# Revit family: Hager-Univers-IP65-D300-H550-Cl.II-encl-PL-en
name_source: partatom
category: Equipement électrique
units: mm (PartAtom-declared; Revit-internal decimal feet)

## family parameters
Configuration du panneau = Deux colonnes, circuits au sein
Cote de connecteur circulaire = Utiliser le diamètre
Couper avec des vides une fois chargée = Non
Hôte = Face
Partagée = Non
Point de calcul de pièce = Non
Type d'élément = Tableau de raccordement

## types (6) — shared parameters
Commentaires du type = Univers
EF000003 - Mounting method = EV000384 - Surface mounted (plaster)
EF000007 - Colour = EV000270 - Grey
EF000040 - Height = 550 mm
EF000049 - Depth = 300 mm  [stored 0.984252 ft]
EF000116 - RAL-number = 7035
EF000118 - With mounting plate = Non
EF000266 - Number of rows = 3
EF001088 - Extension possible = Non
EF001131 - Internal depth = 150 mm  [stored 0.492126 ft]
EF001596 - Material housing = EV000139 - Plastic
EF001613 - Circuit integrity = EV000494 - None
EF003532 - Suitable for outdoor use = Oui
EF004293 - Impact strength = EV008784 - IK10
EF004464 - Type of door = EV002646 - Single
EF005474 - Degree of protection (IP) = EV006421 - IP65
EF006244 - Transparent cover/door = Non
EF006306 - With lock = Oui
EF007800 - Suitable for lightning protection = Oui
EF009170 - Material plate thickness cabinet = 2 mm  [stored 0.00656168 ft]
EF009171 - Material plate thickness door/cover = 2 mm  [stored 0.00656168 ft]
EF009212 - Cover model = EV000116 - Closed
EF015940 - Cover with overpressure release = Non
Fabricant = Hager
HG000002 - With door or cover = Oui
HG000003 - Range = Univers
HG000006 - Flush mounted = Non
HG000009 - Double swing door = Non
HG000010 - Asymmetric doors = Non
HG000023 - Double section enclosure = Non
HG000024 - Bottom section height = 800 mm
HG000026 - Floor standing = Non
zero-valued in all types: EF000218 - Built-in depth, EF000437 - Number of conduit inlets, EF009554 - Number of openings for flange plates, Elévation par défaut, HG000027 - Plinth height

## per-type parameters (varying)
| type | EF000008 - Width | EF000339 - Type of cover | EF002950 - Width in number of modular spacings | EF004427 - Number of modules | EF008873 - Nominal current (In) | HG000004 - Manufacturer reference |
| Surface mounted (plaster) IP65 W1100 H550 D300  - FL34S | 1100 mm | EV001012 - Cover | 48 | 144 | 630 A | FL34S |
| Surface mounted (plaster) IP65 W1100 H550 D300  - FL34SP | 1100 mm | EV001012 - Cover | 48 | 144 | 630 A | FL34SP |
| Surface mounted (plaster) IP65 W600 H550 D300  - FL32S | 600 mm | EV004216 - Door | 24 | 72 | 400 A | FL32S |
| Surface mounted (plaster) IP65 W600 H550 D300  - FL32SP | 600 mm | EV004216 - Door | 24 | 72 | 400 A | FL32SP |
| Surface mounted (plaster) IP65 W850 H550 D300  - FL33S | 850 mm  [stored 2.78871 ft] | EV004216 - Door | 36 | 108 | 630 A | FL33S |
| Surface mounted (plaster) IP65 W850 H550 D300  - FL33SP | 850 mm  [stored 2.78871 ft] | EV004216 - Door | 36 | 108 | 630 A | FL33SP |

note: [stored X ft] marks values corroborated as IEEE doubles in the binary element streams (Revit-internal decimal feet)

## geometry (parser evidence)
native form markers: Sweep x10
no freeform markers — native parametric forms only
